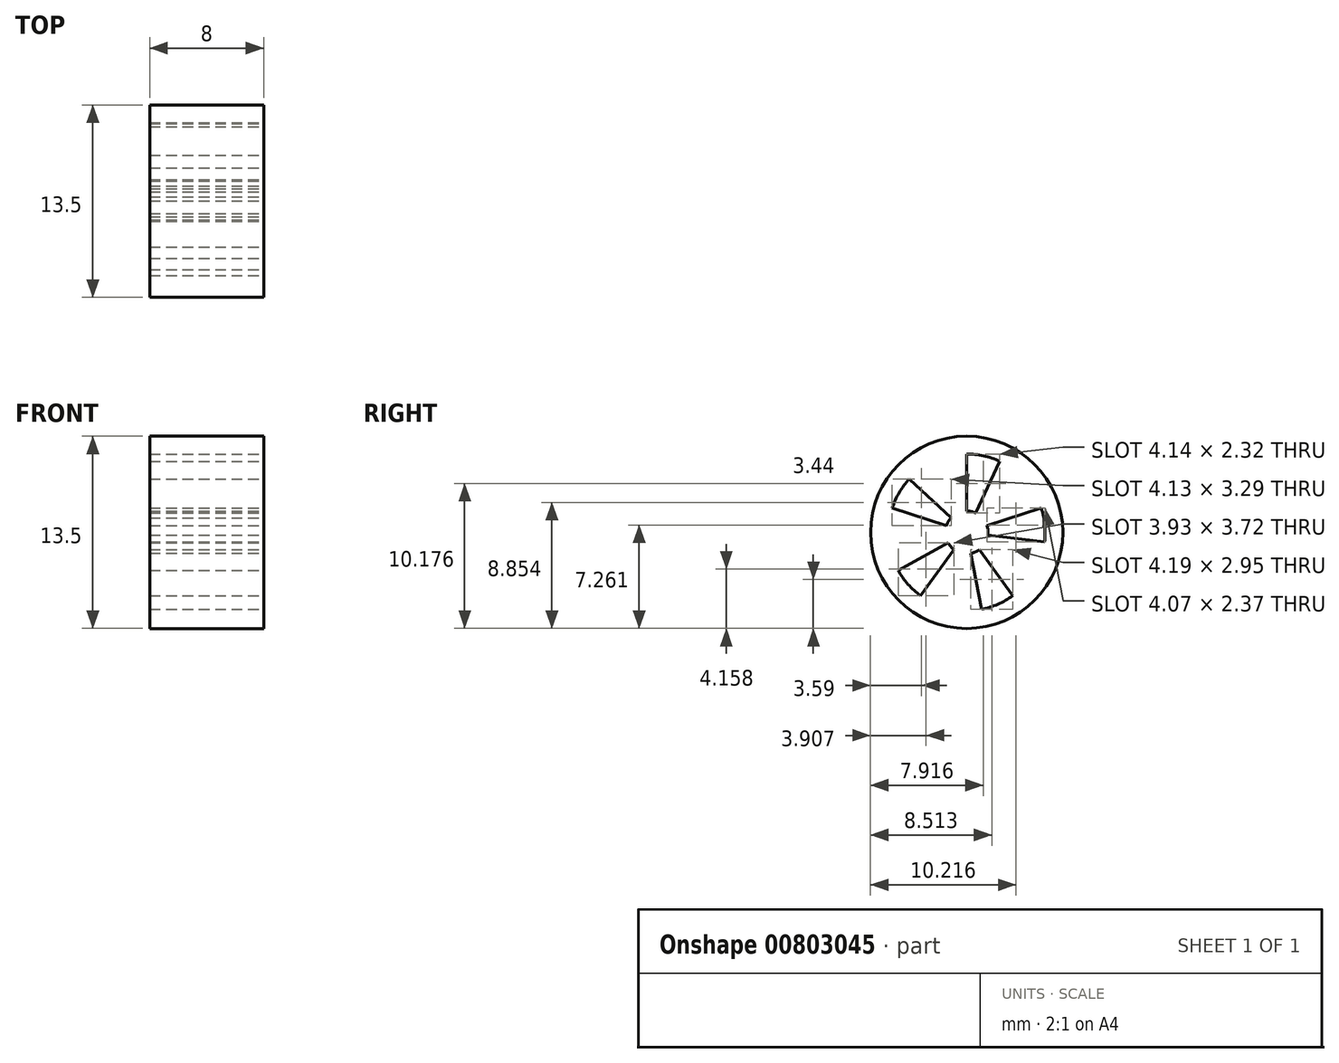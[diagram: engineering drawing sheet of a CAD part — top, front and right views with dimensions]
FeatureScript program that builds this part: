
annotation { "Feature Type Name" : "Feature", "Feature Type Description" : "" }
export const myFeature = defineFeature(function(context is Context, id is Id, definition is map)
    precondition{}
    {
        {
            var Q0;
            Q0=qCreatedBy(makeId("Right.planeOp"),FACE);
            var sketch = newSketch(context, id + "F0", { "sketchPlane" : qUnion([Q0])});
            skCircle(sketch, "E0", {"center": v(-38.79, 29.95) * mm, "radius": 6.75 * mm});
            skSolve(sketch);
        }
        {
            var Q0;
            Q0 = qSketchRegion(id + "F0", true);
            extrude(context, id + "F1", {"entities" : qUnion([Q0]), "depth" : 8 * mm, "offsetDistance" : 25.4 * mm});
        }
        {
            var Q0;
            Q0=makeQuery(id+"F1.opExtrude","CAP_FACE",FACE,{"disambiguationData":[OSD([sQuery(id+"F0.wireOp",EDGE,"E0")])],"isStart":false});
            var sketch = newSketch(context, id + "F2", { "sketchPlane" : qUnion([Q0])});
            skCircle(sketch, "E1", {"center": v(-38.79, 29.95) * mm, "radius": 5.5 * mm});
            skCircle(sketch, "E2", {"center": v(-38.79, 29.95) * mm, "radius": 1.5 * mm});
            skLineSegment(sketch, "E3", {"start": v(-38.79, 31.45) * mm, "end": v(-38.79, 35.45) * mm});
            skLineSegment(sketch, "E4", {"start": v(-38.15, 31.3) * mm, "end": v(-36.46, 34.93) * mm});
            skLineSegment(sketch, "E5.1.0", {"start": v(-40.21, 30.41) * mm, "end": v(-44.02, 31.65) * mm});
            skLineSegment(sketch, "E5.1.1", {"start": v(-39.88, 30.97) * mm, "end": v(-42.8, 33.7) * mm});
            skLineSegment(sketch, "E5.2.0", {"start": v(-39.67, 28.73) * mm, "end": v(-42.02, 25.5) * mm});
            skLineSegment(sketch, "E5.2.1", {"start": v(-40.1, 29.22) * mm, "end": v(-43.6, 27.28) * mm});
            skLineSegment(sketch, "E5.3.0", {"start": v(-37.9, 28.73) * mm, "end": v(-35.55, 25.5) * mm});
            skLineSegment(sketch, "E5.3.1", {"start": v(-38.5, 28.47) * mm, "end": v(-37.74, 24.55) * mm});
            skLineSegment(sketch, "E5.4.0", {"start": v(-37.36, 30.41) * mm, "end": v(-33.56, 31.65) * mm});
            skLineSegment(sketch, "E5.4.1", {"start": v(-37.3, 29.76) * mm, "end": v(-33.33, 29.28) * mm});
            skSolve(sketch);
        }
        {
            var Q0;
            {var subQ0=sQuery(id+"F2.wireOp",EDGE,"E3");Q0=makeQuery(id+"F2.imprint","IMPRINT",FACE,{"disambiguationData":[TD([[makeQuery(id+"F2.imprint","IMPRINT",EDGE,{"derivedFrom":subQ0}),-1.0]])]});}
            var Q1;
            {var subQ0=sQuery(id+"F2.wireOp",EDGE,"E5.1.0");Q1=makeQuery(id+"F2.imprint","IMPRINT",FACE,{"disambiguationData":[TD([[makeQuery(id+"F2.imprint","IMPRINT",EDGE,{"derivedFrom":subQ0}),-1.0]])]});}
            var Q2;
            {var subQ0=sQuery(id+"F2.wireOp",EDGE,"E5.2.0");Q2=makeQuery(id+"F2.imprint","IMPRINT",FACE,{"disambiguationData":[TD([[makeQuery(id+"F2.imprint","IMPRINT",EDGE,{"derivedFrom":subQ0}),-1.0]])]});}
            var Q3;
            {var subQ0=sQuery(id+"F2.wireOp",EDGE,"E5.3.0");Q3=makeQuery(id+"F2.imprint","IMPRINT",FACE,{"disambiguationData":[TD([[makeQuery(id+"F2.imprint","IMPRINT",EDGE,{"derivedFrom":subQ0}),-1.0]])]});}
            var Q4;
            {var subQ0=sQuery(id+"F2.wireOp",EDGE,"E5.4.0");Q4=makeQuery(id+"F2.imprint","IMPRINT",FACE,{"disambiguationData":[TD([[makeQuery(id+"F2.imprint","IMPRINT",EDGE,{"derivedFrom":subQ0}),-1.0]])]});}
            extrude(context, id + "F3", {"entities" : qUnion([Q0, Q1, Q2, Q3, Q4]), "operationType" : NewBodyOperationType.REMOVE, "endBound" : BoundingType.THROUGH_ALL, "oppositeDirection" : true, "depth" : 25.4 * mm, "offsetDistance" : 25.4 * mm});
        }
    });
